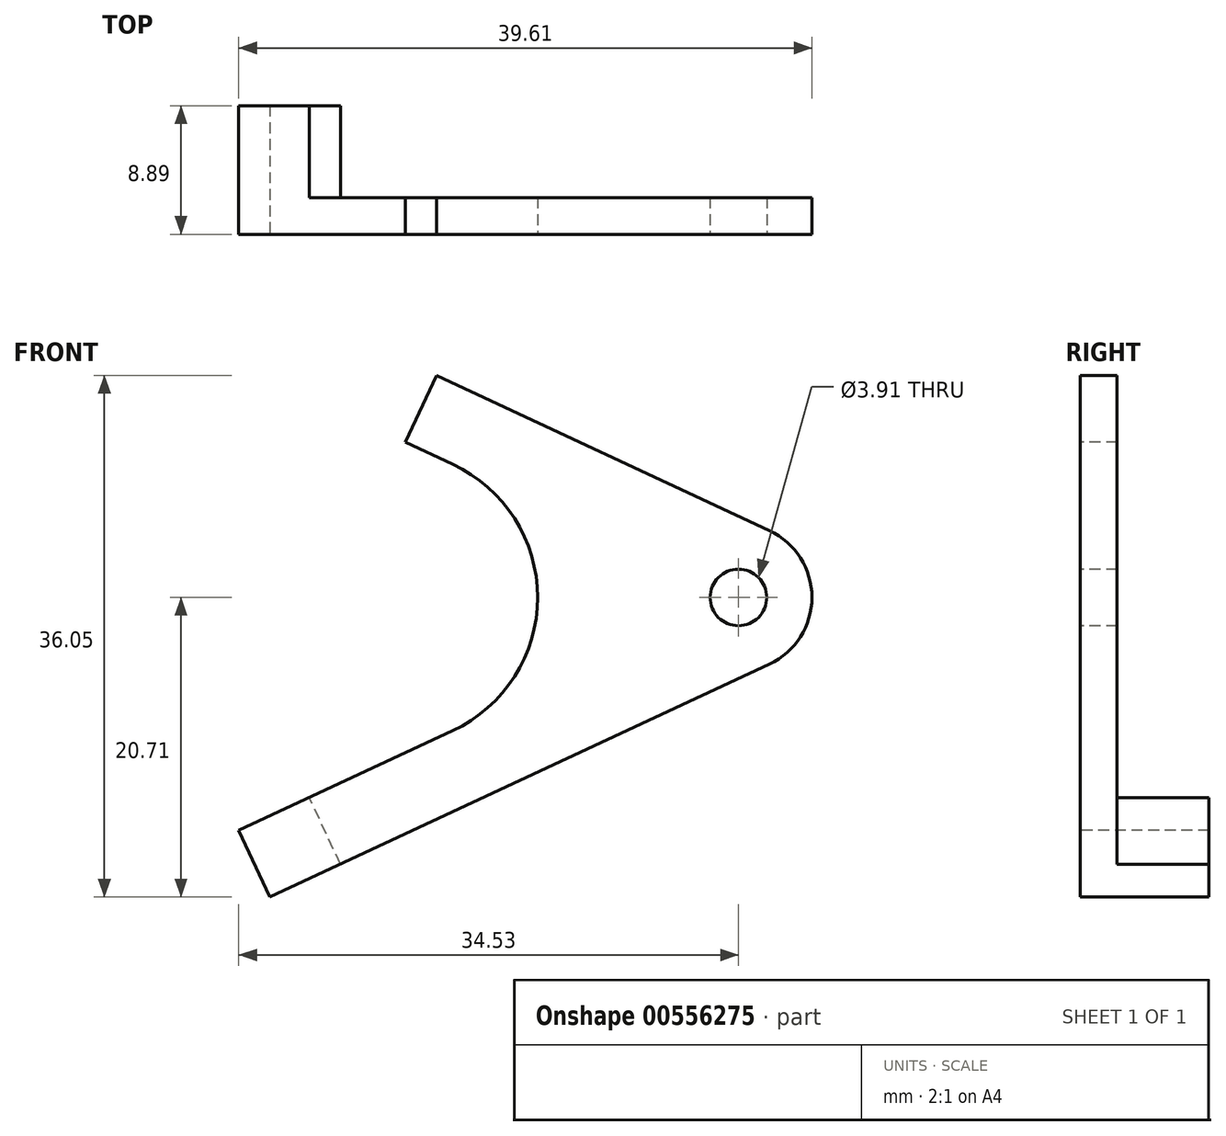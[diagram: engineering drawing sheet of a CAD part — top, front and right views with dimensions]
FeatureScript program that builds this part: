
annotation { "Feature Type Name" : "Feature", "Feature Type Description" : "" }
export const myFeature = defineFeature(function(context is Context, id is Id, definition is map)
    precondition{}
    {
        {
            var Q0;
            Q0=qCreatedBy(makeId("Front.planeOp"),FACE);
            var sketch = newSketch(context, id + "F0", { "sketchPlane" : qUnion([Q0])});
            skCircle(sketch, "E0", {"center": v(0, 0) * mm, "radius": 1.96 * mm});
            skLineSegment(sketch, "E1", {"start": v(2.15, 4.6) * mm, "end": v(-20.87, 15.34) * mm});
            skLineSegment(sketch, "E2", {"start": v(-20.87, 15.34) * mm, "end": v(-23.02, 10.73) * mm});
            skLineSegment(sketch, "E3", {"start": v(-34.53, -16.1) * mm, "end": v(-32.38, -20.7) * mm});
            skLineSegment(sketch, "E4", {"start": v(-32.38, -20.7) * mm, "end": v(2.15, -4.6) * mm});
            skLineSegment(sketch, "E5", {"start": v(0, 0) * mm, "end": v(2.15, -4.6) * mm, "construction": true});
            skLineSegment(sketch, "E6", {"start": v(0, 0) * mm, "end": v(2.15, 4.6) * mm, "construction": true});
            skLineSegment(sketch, "E7", {"start": v(0, 0) * mm, "end": v(0, 0) * mm});
            skLineSegment(sketch, "E8", {"start": v(-19.75, 9.2) * mm, "end": v(-23.02, 10.73) * mm});
            skLineSegment(sketch, "E9", {"start": v(-19.75, -9.2) * mm, "end": v(-34.53, -16.1) * mm});
            skPoint(sketch, "E10.visualSharp", {"position": v(12.02, 0) * mm});
            skArc(sketch, "E10.filletArc", {"start": v(2.15, -4.6) * mm, "mid": v(5.08, 0) * mm, "end": v(2.15, 4.6) * mm});
            skArc(sketch, "E11.filletArc", {"start": v(-19.75, -9.2) * mm, "mid": v(-13.88, 0) * mm, "end": v(-19.75, 9.2) * mm});
            skSolve(sketch);
        }
        {
            var Q0;
            Q0 = qSketchRegion(id + "F0", true);
            extrude(context, id + "F1", {"entities" : qUnion([Q0]), "oppositeDirection" : true, "depth" : 2.54 * mm, "offsetDistance" : 25.4 * mm});
        }
        {
            var Q0;
            Q0=makeQuery(id+"F1.opExtrude","CAP_FACE",FACE,{"disambiguationData":[OSD([sQuery(id+"F0.wireOp",EDGE,"E0"),sQuery(id+"F0.wireOp",EDGE,"E1"),sQuery(id+"F0.wireOp",EDGE,"E2"),sQuery(id+"F0.wireOp",EDGE,"E3"),sQuery(id+"F0.wireOp",EDGE,"E4"),sQuery(id+"F0.wireOp",EDGE,"E8"),sQuery(id+"F0.wireOp",EDGE,"E9"),sQuery(id+"F0.wireOp",EDGE,"E10.filletArc"),sQuery(id+"F0.wireOp",EDGE,"E11.filletArc")])],"isStart":false});
            var sketch = newSketch(context, id + "F2", { "sketchPlane" : qUnion([Q0])});
            skLineSegment(sketch, "E12", {"start": v(34.53, -16.1) * mm, "end": v(32.38, -20.7) * mm});
            skLineSegment(sketch, "E13", {"start": v(32.38, -20.7) * mm, "end": v(27.51, -18.43) * mm});
            skLineSegment(sketch, "E14", {"start": v(27.51, -18.43) * mm, "end": v(29.66, -13.83) * mm});
            skLineSegment(sketch, "E15", {"start": v(29.66, -13.83) * mm, "end": v(34.53, -16.1) * mm});
            skSolve(sketch);
        }
        {
            var Q0;
            Q0 = qSketchRegion(id + "F2", true);
            extrude(context, id + "F3", {"entities" : qUnion([Q0]), "operationType" : NewBodyOperationType.ADD, "depth" : 6.35 * mm, "offsetDistance" : 25.4 * mm});
        }
    });
